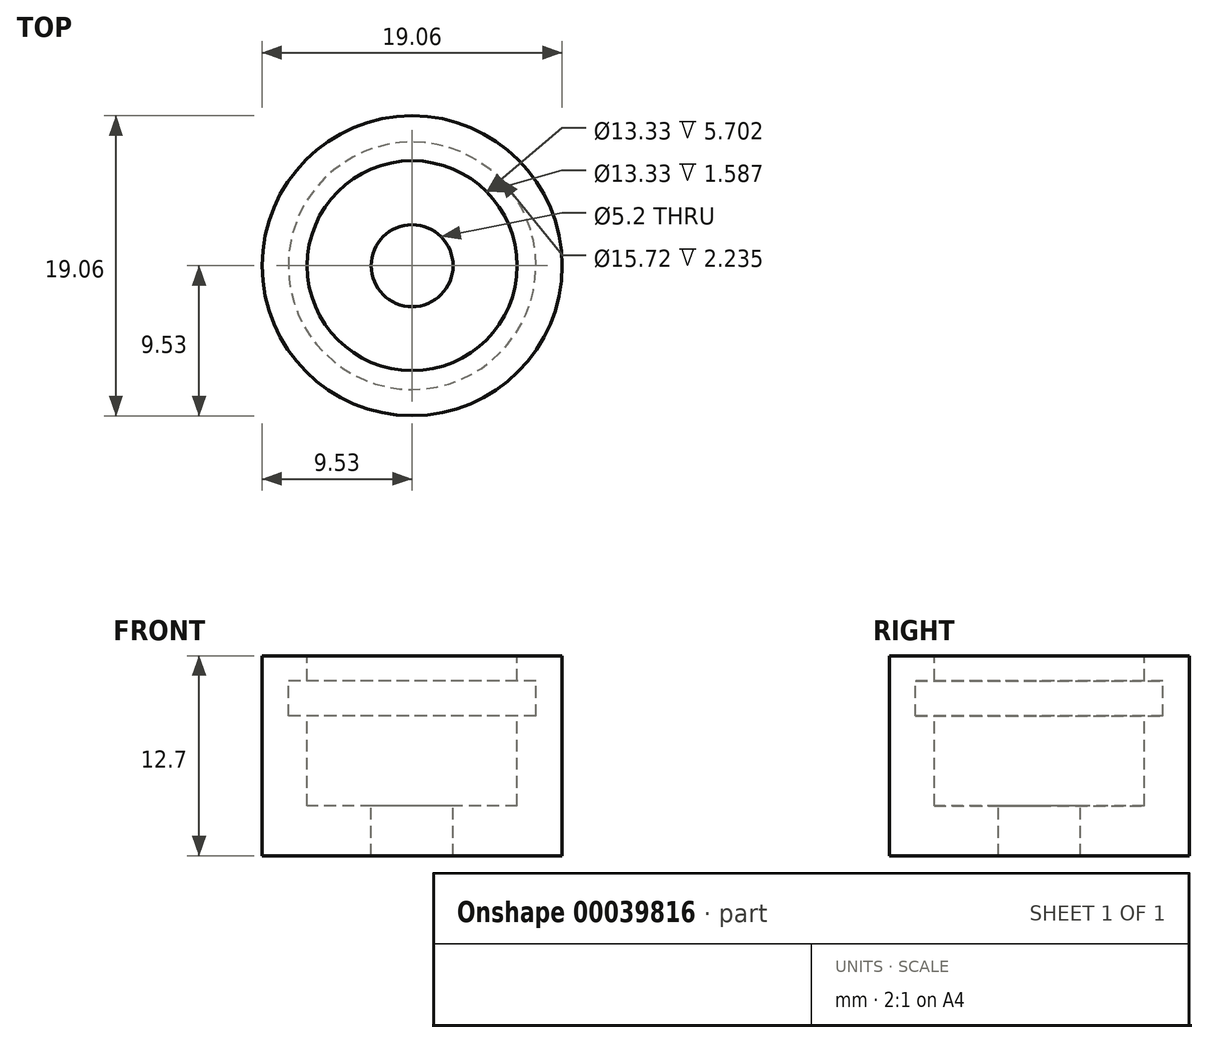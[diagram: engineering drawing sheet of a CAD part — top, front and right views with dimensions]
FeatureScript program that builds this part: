
annotation { "Feature Type Name" : "Feature", "Feature Type Description" : "" }
export const myFeature = defineFeature(function(context is Context, id is Id, definition is map)
    precondition{}
    {
        {
            var Q0;
            Q0=qCreatedBy(makeId("Top.planeOp"),FACE);
            var sketch = newSketch(context, id + "F0", { "sketchPlane" : qUnion([Q0])});
            skCircle(sketch, "E0", {"center": v(0, 0) * mm, "radius": 9.53 * mm});
            skSolve(sketch);
        }
        {
            var Q0;
            Q0 = qSketchRegion(id + "F0", true);
            extrude(context, id + "F1", {"entities" : qUnion([Q0]), "depth" : 12.7 * mm});
        }
        {
            var Q0;
            Q0=makeQuery(id+"F1.opExtrude","CAP_FACE",FACE,{"disambiguationData":[OSD([sQuery(id+"F0.wireOp",EDGE,"E0")])],"isStart":false});
            var sketch = newSketch(context, id + "F2", { "sketchPlane" : qUnion([Q0])});
            skCircle(sketch, "E1", {"center": v(0, 0) * mm, "radius": 6.67 * mm});
            skSolve(sketch);
        }
        {
            var Q0;
            Q0 = qSketchRegion(id + "F2", true);
            extrude(context, id + "F3", {"entities" : qUnion([Q0]), "operationType" : NewBodyOperationType.REMOVE, "oppositeDirection" : true, "depth" : 9.52 * mm});
        }
        {
            var Q0;
            Q0=makeQuery(id+"F3.boolean.opBoolean","COPY",FACE,{"derivedFrom":makeQuery(id+"F3.opExtrude","CAP_FACE",FACE,{"disambiguationData":[OSD([sQuery(id+"F2.wireOp",EDGE,"E1")])],"isStart":false})});
            var sketch = newSketch(context, id + "F4", { "sketchPlane" : qUnion([Q0])});
            skCircle(sketch, "E2", {"center": v(0, 0) * mm, "radius": 2.6 * mm});
            skSolve(sketch);
        }
        {
            var Q0;
            Q0 = qSketchRegion(id + "F4", true);
            extrude(context, id + "F5", {"entities" : qUnion([Q0]), "operationType" : NewBodyOperationType.REMOVE, "oppositeDirection" : true, "depth" : 25.4 * mm});
        }
        {
            var Q0;
            Q0=qCreatedBy(makeId("Front.planeOp"),FACE);
            var sketch = newSketch(context, id + "F6", { "sketchPlane" : qUnion([Q0])});
            skLineSegment(sketch, "E3.bottom", {"start": v(6.67, 11.11) * mm, "end": v(7.86, 11.11) * mm});
            skLineSegment(sketch, "E3.top", {"start": v(6.67, 8.88) * mm, "end": v(7.86, 8.88) * mm});
            skLineSegment(sketch, "E3.left", {"start": v(6.67, 11.11) * mm, "end": v(6.67, 8.88) * mm});
            skLineSegment(sketch, "E3.right", {"start": v(7.86, 11.11) * mm, "end": v(7.86, 8.88) * mm});
            skLineSegment(sketch, "E4", {"start": v(0, 0) * mm, "end": v(0, 38.04) * mm, "construction": true});
            skSolve(sketch);
        }
        {
            var Q0;
            Q0 = qSketchRegion(id + "F6", true);
            var Q1;
            Q1=sQuery(id+"F6.wireOp",EDGE,"E4");
            revolve(context, id + "F7", {"operationType" : NewBodyOperationType.REMOVE, "entities" : qUnion([Q0]), "axis" : qUnion([Q1]), "revolveType" : RevolveType.FULL, "oppositeDirection" : true});
        }
    });
